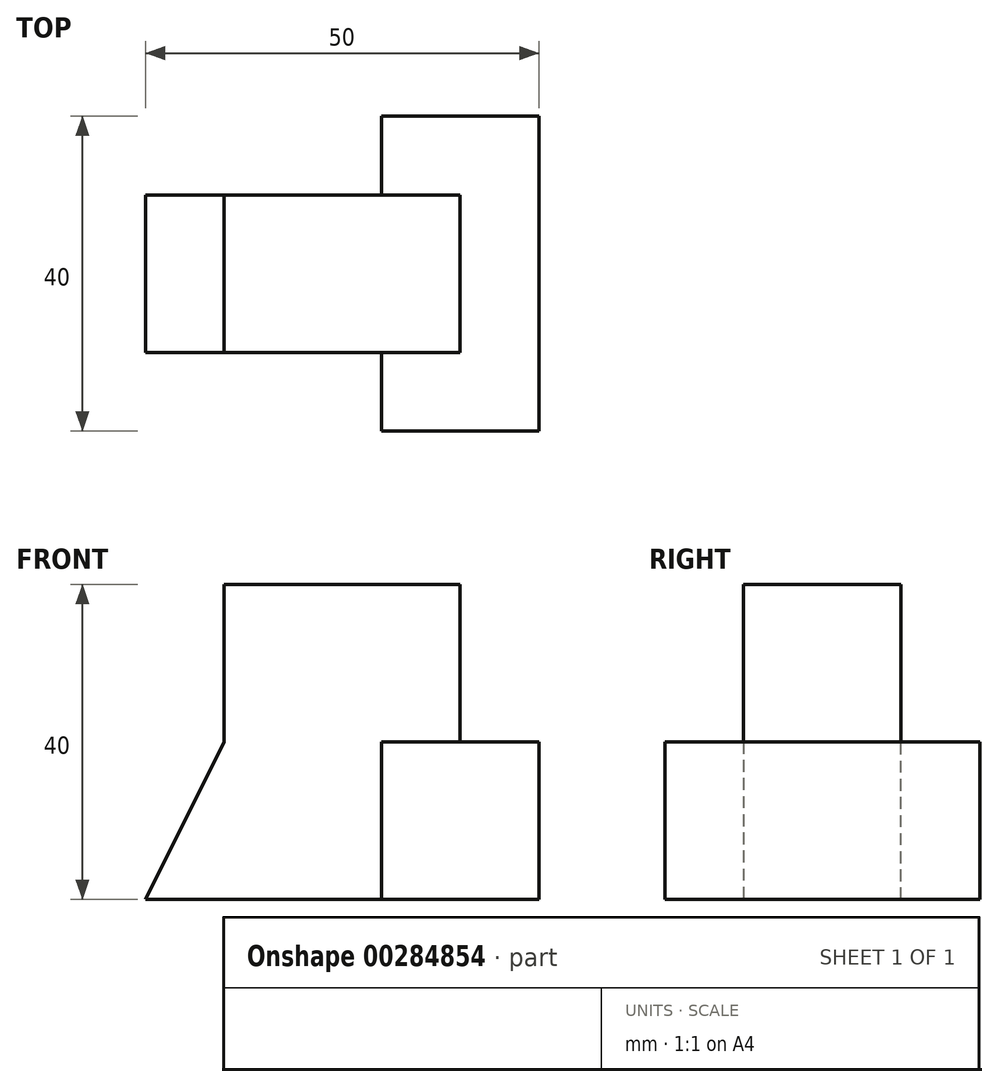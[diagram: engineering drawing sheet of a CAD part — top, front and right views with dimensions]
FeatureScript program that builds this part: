
annotation { "Feature Type Name" : "Feature", "Feature Type Description" : "" }
export const myFeature = defineFeature(function(context is Context, id is Id, definition is map)
    precondition{}
    {
        {
            var Q0;
            Q0=qCreatedBy(makeId("Front.planeOp"),FACE);
            var sketch = newSketch(context, id + "F0", { "sketchPlane" : qUnion([Q0])});
            skLineSegment(sketch, "E0.bottom", {"start": v(0, 0) * mm, "end": v(50, 0) * mm});
            skLineSegment(sketch, "E0.top", {"start": v(0, 40) * mm, "end": v(50, 40) * mm});
            skLineSegment(sketch, "E0.left", {"start": v(0, 0) * mm, "end": v(0, 40) * mm});
            skLineSegment(sketch, "E0.right", {"start": v(50, 0) * mm, "end": v(50, 40) * mm});
            skSolve(sketch);
        }
        {
            var Q0;
            Q0=makeQuery(id+"F0.imprint","IMPRINT",FACE,{"disambiguationData":[TD([[makeQuery(id+"F0.imprint","IMPRINT",EDGE,{"derivedFrom":sQuery(id+"F0.wireOp",EDGE,"E0.bottom")}),1.0]])]});
            extrude(context, id + "F1", {"entities" : qUnion([Q0]), "depth" : 40 * mm});
        }
        {
            var Q0;
            Q0=makeQuery(id+"F1.opExtrude","SWEPT_FACE",FACE,{"disambiguationData":[OSD([sQuery(id+"F0.wireOp",EDGE,"E0.left")])]});
            var sketch = newSketch(context, id + "F2", { "sketchPlane" : qUnion([Q0])});
            skLineSegment(sketch, "E1", {"start": v(0, 20) * mm, "end": v(40, 20) * mm});
            skLineSegment(sketch, "E2", {"start": v(30, 40) * mm, "end": v(30, 20) * mm});
            skLineSegment(sketch, "E3", {"start": v(10, 40) * mm, "end": v(10, 20) * mm});
            skLineSegment(sketch, "E4.0", {"start": v(40, 40) * mm, "end": v(0, 40) * mm});
            skLineSegment(sketch, "E5.0.1", {"start": v(40, 40) * mm, "end": v(40, 20) * mm});
            skLineSegment(sketch, "E5.0.3", {"start": v(40, 20) * mm, "end": v(40, 40) * mm});
            skLineSegment(sketch, "E6.0.1", {"start": v(0, 40) * mm, "end": v(0, 20) * mm});
            skLineSegment(sketch, "E6.0.3", {"start": v(0, 0) * mm, "end": v(0, 40) * mm});
            skPoint(sketch, "E7.orphan", {"position": v(40, 0) * mm});
            skPoint(sketch, "E8.orphan", {"position": v(0, 0) * mm});
            skSolve(sketch);
        }
        {
            var Q0;
            {var subQ3=sQuery(id+"F2.wireOp",EDGE,"E3");Q0=makeQuery(id+"F2.imprint","IMPRINT",FACE,{"disambiguationData":[TD([[makeQuery(id+"F2.imprint","IMPRINT",EDGE,{"derivedFrom":subQ3}),-1.0]])]});}
            var Q1;
            {var subQ2=sQuery(id+"F2.wireOp",EDGE,"E2");Q1=makeQuery(id+"F2.imprint","IMPRINT",FACE,{"disambiguationData":[TD([[makeQuery(id+"F2.imprint","IMPRINT",EDGE,{"derivedFrom":subQ2}),1.0]])]});}
            extrude(context, id + "F3", {"entities" : qUnion([Q0, Q1]), "operationType" : NewBodyOperationType.REMOVE, "endBound" : BoundingType.THROUGH_ALL, "oppositeDirection" : true, "depth" : 30 * mm});
        }
        {
            var Q0;
            {var subQ0=sQuery(id+"F2.wireOp",EDGE,"E1");Q0=makeQuery(id+"F3.boolean.opBoolean","COPY",FACE,{"derivedFrom":makeQuery(id+"F3.opExtrude","SWEPT_FACE",FACE,{"disambiguationData":[OSD([subQ0]),TDD([makeQuery(id+"F2.imprint","IMPRINT",EDGE,{"disambiguationData":[TD([[makeQuery(id+"F2.imprint","INTERSECT",VERTEX,{"derivedFrom":[subQ0,sQuery(id+"F2.wireOp",EDGE,"E6.0.3")]}),-1.0]])],"derivedFrom":subQ0})])]})});}
            var sketch = newSketch(context, id + "F4", { "sketchPlane" : qUnion([Q0])});
            skLineSegment(sketch, "E9.0", {"start": v(50, 0) * mm, "end": v(30, 0) * mm});
            skLineSegment(sketch, "E10.0", {"start": v(50, -10) * mm, "end": v(30, -10) * mm});
            skLineSegment(sketch, "E11.0", {"start": v(50, -30) * mm, "end": v(30, -30) * mm});
            skLineSegment(sketch, "E12.0", {"start": v(50, -40) * mm, "end": v(30, -40) * mm});
            skLineSegment(sketch, "E13", {"start": v(30, 0) * mm, "end": v(30, -10) * mm});
            skLineSegment(sketch, "E14", {"start": v(30, -30) * mm, "end": v(30, -40) * mm});
            skLineSegment(sketch, "E15.0", {"start": v(50, -30) * mm, "end": v(50, -40) * mm});
            skLineSegment(sketch, "E16.0", {"start": v(50, 0) * mm, "end": v(50, -10) * mm});
            skPoint(sketch, "E17.orphan", {"position": v(0, -10) * mm});
            skPoint(sketch, "E18.orphan", {"position": v(0, -30) * mm});
            skPoint(sketch, "E19.orphan", {"position": v(0, -40) * mm});
            skPoint(sketch, "E20.orphan", {"position": v(0, 0) * mm});
            skLineSegment(sketch, "E21.0", {"start": v(50, 0) * mm, "end": v(0, 0) * mm});
            skLineSegment(sketch, "E22.0", {"start": v(50, -10) * mm, "end": v(0, -10) * mm});
            skLineSegment(sketch, "E23.0", {"start": v(0, 0) * mm, "end": v(0, -10) * mm});
            skLineSegment(sketch, "E24.0", {"start": v(0, -30) * mm, "end": v(0, -40) * mm});
            skLineSegment(sketch, "E25.0", {"start": v(50, -40) * mm, "end": v(0, -40) * mm});
            skLineSegment(sketch, "E26.0", {"start": v(50, -30) * mm, "end": v(0, -30) * mm});
            skSolve(sketch);
        }
        {
            var Q0;
            {var subQ0=sQuery(id+"F4.wireOp",EDGE,"E13");Q0=makeQuery(id+"F4.imprint","IMPRINT",FACE,{"disambiguationData":[TD([[makeQuery(id+"F4.imprint","IMPRINT",EDGE,{"derivedFrom":subQ0}),-1.0]])]});}
            var Q1;
            {var subQ0=sQuery(id+"F4.wireOp",EDGE,"E14");Q1=makeQuery(id+"F4.imprint","IMPRINT",FACE,{"disambiguationData":[TD([[makeQuery(id+"F4.imprint","IMPRINT",EDGE,{"derivedFrom":subQ0}),-1.0]])]});}
            extrude(context, id + "F5", {"entities" : qUnion([Q0, Q1]), "operationType" : NewBodyOperationType.REMOVE, "endBound" : BoundingType.THROUGH_ALL, "oppositeDirection" : true, "depth" : 25 * mm});
        }
        {
            var Q0;
            Q0=makeQuery(id+"F1.opExtrude","SWEPT_FACE",FACE,{"disambiguationData":[OSD([sQuery(id+"F0.wireOp",EDGE,"E0.top")])]});
            var sketch = newSketch(context, id + "F6", { "sketchPlane" : qUnion([Q0])});
            skLineSegment(sketch, "E27", {"start": v(40, -10) * mm, "end": v(40, -30) * mm});
            skLineSegment(sketch, "E28.0", {"start": v(50, -10) * mm, "end": v(0, -10) * mm});
            skLineSegment(sketch, "E29.0", {"start": v(50, -30) * mm, "end": v(50, -10) * mm});
            skLineSegment(sketch, "E30.0", {"start": v(50, -30) * mm, "end": v(0, -30) * mm});
            skSolve(sketch);
        }
        {
            var Q0;
            Q0=qSketchRegion(id+"F6",true);
            var Q1;
            {var subQ0=sQuery(id+"F2.wireOp",EDGE,"E1");Q1=makeQuery(id+"F3.boolean.opBoolean","COPY",FACE,{"derivedFrom":makeQuery(id+"F3.opExtrude","SWEPT_FACE",FACE,{"disambiguationData":[OSD([subQ0]),TDD([makeQuery(id+"F2.imprint","IMPRINT",EDGE,{"disambiguationData":[TD([[makeQuery(id+"F2.imprint","INTERSECT",VERTEX,{"derivedFrom":[subQ0,sQuery(id+"F2.wireOp",EDGE,"E6.0.3")]}),-1.0]])],"derivedFrom":subQ0})])]})});}
            extrude(context, id + "F7", {"entities" : qUnion([Q0]), "operationType" : NewBodyOperationType.REMOVE, "endBound" : BoundingType.UP_TO_SURFACE, "oppositeDirection" : true, "endBoundEntityFace" : qUnion([Q1]), "depth" : 25 * mm});
        }
        {
            var Q0;
            Q0=makeQuery(id+"F5.boolean.opBoolean","MERGE",FACE,{"derivedFrom":[makeQuery(id+"F3.boolean.opBoolean","COPY",FACE,{"derivedFrom":makeQuery(id+"F3.opExtrude","SWEPT_FACE",FACE,{"disambiguationData":[OSD([sQuery(id+"F2.wireOp",EDGE,"E2")])]})}),makeQuery(id+"F5.opExtrude","SWEPT_FACE",FACE,{"disambiguationData":[OSD([sQuery(id+"F4.wireOp",EDGE,"E26.0")])]})]});
            var sketch = newSketch(context, id + "F8", { "sketchPlane" : qUnion([Q0])});
            skLineSegment(sketch, "E31.bottom", {"start": v(0, 40) * mm, "end": v(10, 40) * mm});
            skLineSegment(sketch, "E31.top", {"start": v(0, 20) * mm, "end": v(10, 20) * mm});
            skLineSegment(sketch, "E31.left", {"start": v(0, 40) * mm, "end": v(0, 20) * mm});
            skLineSegment(sketch, "E31.right", {"start": v(10, 40) * mm, "end": v(10, 20) * mm});
            skLineSegment(sketch, "E32", {"start": v(10, 20) * mm, "end": v(0, 0) * mm});
            skLineSegment(sketch, "E33", {"start": v(0, 0) * mm, "end": v(0, 20) * mm});
            skSolve(sketch);
        }
        {
            var Q0;
            Q0=qSketchRegion(id+"F8",true);
            extrude(context, id + "F9", {"entities" : qUnion([Q0]), "operationType" : NewBodyOperationType.REMOVE, "endBound" : BoundingType.THROUGH_ALL, "oppositeDirection" : true, "depth" : 25 * mm});
        }
    });
